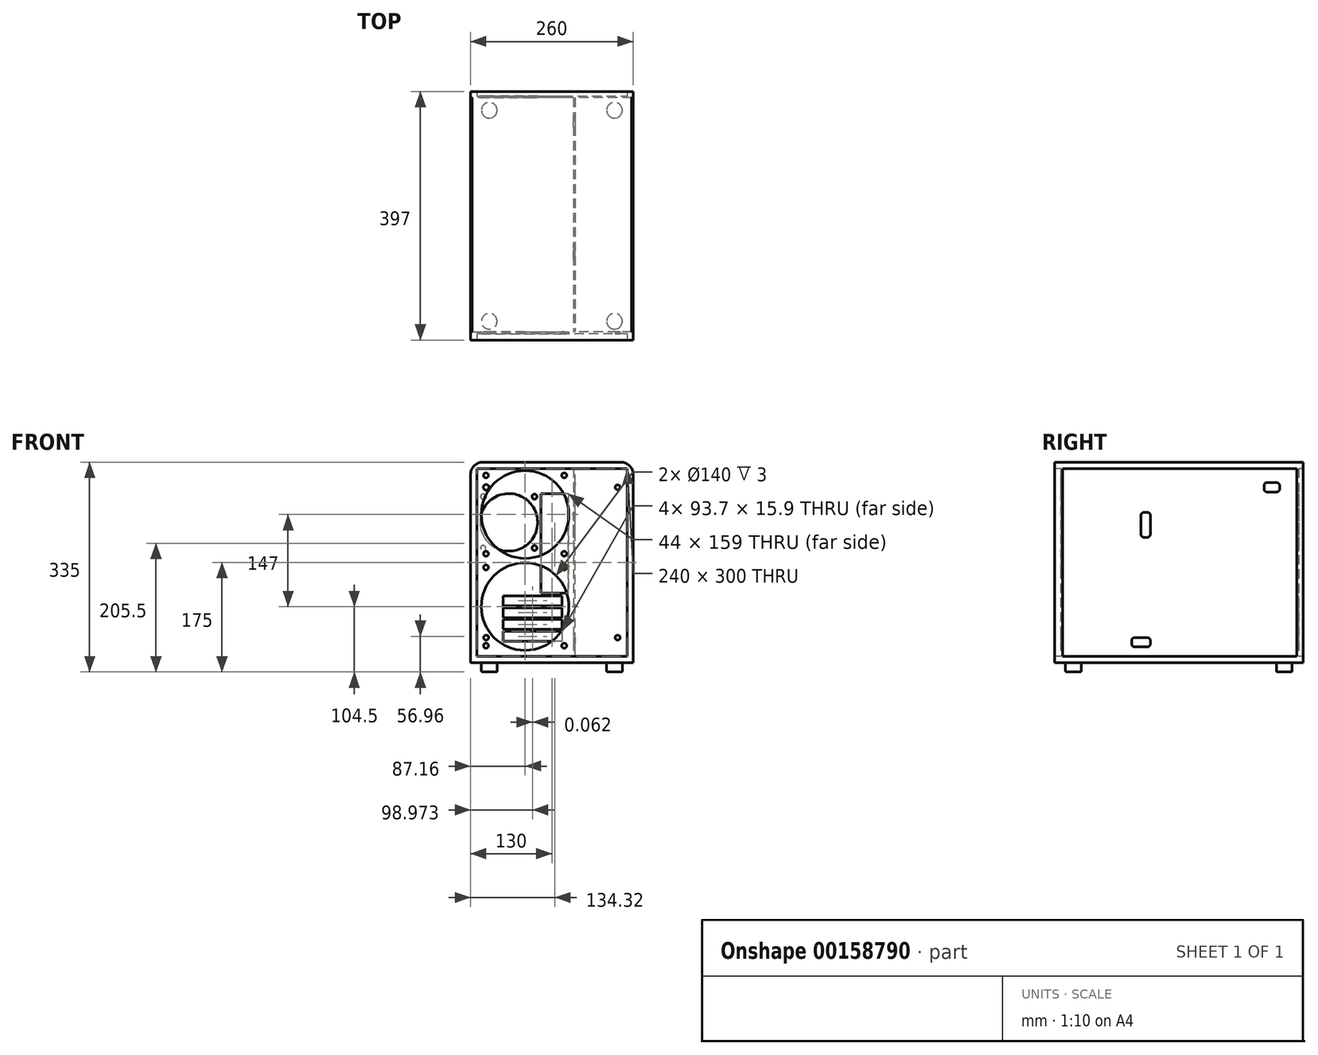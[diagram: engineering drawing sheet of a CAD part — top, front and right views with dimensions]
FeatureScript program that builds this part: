
annotation { "Feature Type Name" : "Feature", "Feature Type Description" : "" }
export const myFeature = defineFeature(function(context is Context, id is Id, definition is map)
    precondition{}
    {
        {
            var Q0;
            Q0=qCreatedBy(makeId("Top.planeOp"),FACE);
            var sketch = newSketch(context, id + "F0", { "sketchPlane" : qUnion([Q0])});
            skLineSegment(sketch, "E0.bottom", {"start": v(130, 198.5) * mm, "end": v(-130, 198.5) * mm});
            skLineSegment(sketch, "E0.top", {"start": v(130, -198.5) * mm, "end": v(-130, -198.5) * mm});
            skLineSegment(sketch, "E0.left", {"start": v(130, 198.5) * mm, "end": v(130, -198.5) * mm});
            skLineSegment(sketch, "E0.right", {"start": v(-130, 198.5) * mm, "end": v(-130, -198.5) * mm});
            skPoint(sketch, "E0.middle", {"position": v(0, 0) * mm});
            skSolve(sketch);
        }
        {
            var Q0;
            Q0=makeQuery(id+"F0.imprint","IMPRINT",FACE,{"disambiguationData":[TD([[makeQuery(id+"F0.imprint","IMPRINT",EDGE,{"derivedFrom":sQuery(id+"F0.wireOp",EDGE,"E0.bottom")}),1.0]])]});
            extrude(context, id + "F1", {"entities" : qUnion([Q0]), "depth" : 320 * mm});
        }
        {
            var Q0;
            Q0=makeQuery(id+"F1.opExtrude","SWEPT_FACE",FACE,{"disambiguationData":[OSD([sQuery(id+"F0.wireOp",EDGE,"E0.top")])]});
            var sketch = newSketch(context, id + "F2", { "sketchPlane" : qUnion([Q0])});
            skLineSegment(sketch, "E1.bottom", {"start": v(120, 310) * mm, "end": v(-120, 310) * mm});
            skLineSegment(sketch, "E1.top", {"start": v(120, 10) * mm, "end": v(-120, 10) * mm});
            skLineSegment(sketch, "E1.left", {"start": v(120, 310) * mm, "end": v(120, 10) * mm});
            skLineSegment(sketch, "E1.right", {"start": v(-120, 310) * mm, "end": v(-120, 10) * mm});
            skPoint(sketch, "E1.middle", {"position": v(0, 160) * mm});
            skSolve(sketch);
        }
        {
            var Q0;
            Q0 = qSketchRegion(id + "F2", true);
            extrude(context, id + "F3", {"entities" : qUnion([Q0]), "operationType" : NewBodyOperationType.REMOVE, "oppositeDirection" : true, "depth" : 506.73 * mm});
        }
        {
            var Q0;
            Q0=makeQuery(id+"F1.opExtrude","SWEPT_FACE",FACE,{"disambiguationData":[OSD([sQuery(id+"F0.wireOp",EDGE,"E0.right")])]});
            var sketch = newSketch(context, id + "F4", { "sketchPlane" : qUnion([Q0])});
            skLineSegment(sketch, "E2.bottom", {"start": v(188.5, 310) * mm, "end": v(-188.5, 310) * mm});
            skLineSegment(sketch, "E2.top", {"start": v(188.5, 10) * mm, "end": v(-188.5, 10) * mm});
            skLineSegment(sketch, "E2.left", {"start": v(188.5, 310) * mm, "end": v(188.5, 10) * mm});
            skLineSegment(sketch, "E2.right", {"start": v(-188.5, 310) * mm, "end": v(-188.5, 10) * mm});
            skPoint(sketch, "E2.middle", {"position": v(0, 160) * mm});
            skLineSegment(sketch, "E3", {"start": v(0, 0) * mm, "end": v(0, 10) * mm});
            skSolve(sketch);
        }
        {
            var Q0;
            Q0 = qSketchRegion(id + "F4", true);
            extrude(context, id + "F5", {"entities" : qUnion([Q0]), "operationType" : NewBodyOperationType.REMOVE, "oppositeDirection" : true, "depth" : 304.8 * mm});
        }
        {
            var Q0;
            Q0=makeQuery(id+"F5.boolean.opBoolean","MERGE",FACE,{"derivedFrom":[makeQuery(id+"F3.boolean.opBoolean","COPY",FACE,{"derivedFrom":makeQuery(id+"F3.opExtrude","SWEPT_FACE",FACE,{"disambiguationData":[OSD([sQuery(id+"F2.wireOp",EDGE,"E1.top")])]})}),makeQuery(id+"F5.opExtrude","SWEPT_FACE",FACE,{"disambiguationData":[OSD([sQuery(id+"F4.wireOp",EDGE,"E2.top")])]})]});
            var sketch = newSketch(context, id + "F6", { "sketchPlane" : qUnion([Q0])});
            skLineSegment(sketch, "E4.bottom", {"start": v(-127.3, -188.5) * mm, "end": v(-124.3, -188.5) * mm});
            skLineSegment(sketch, "E4.top", {"start": v(-127.3, 188.5) * mm, "end": v(-124.3, 188.5) * mm});
            skLineSegment(sketch, "E4.left", {"start": v(-127.3, -188.5) * mm, "end": v(-127.3, 188.5) * mm});
            skLineSegment(sketch, "E4.right", {"start": v(-124.3, -188.5) * mm, "end": v(-124.3, 188.5) * mm});
            skLineSegment(sketch, "E5.bottom", {"start": v(127.32, 188.5) * mm, "end": v(124.32, 188.5) * mm});
            skLineSegment(sketch, "E5.top", {"start": v(127.32, -188.5) * mm, "end": v(124.32, -188.5) * mm});
            skLineSegment(sketch, "E5.left", {"start": v(127.32, 188.5) * mm, "end": v(127.32, -188.5) * mm});
            skLineSegment(sketch, "E5.right", {"start": v(124.32, 188.5) * mm, "end": v(124.32, -188.5) * mm});
            skSolve(sketch);
        }
        {
            var Q0;
            Q0 = qSketchRegion(id + "F6", true);
            extrude(context, id + "F7", {"entities" : qUnion([Q0]), "operationType" : NewBodyOperationType.ADD, "depth" : 300 * mm});
        }
        {
            var Q0;
            Q0=makeQuery(id+"F1.opExtrude","CAP_FACE",FACE,{"disambiguationData":[OSD([sQuery(id+"F0.wireOp",EDGE,"E0.bottom"),sQuery(id+"F0.wireOp",EDGE,"E0.top"),sQuery(id+"F0.wireOp",EDGE,"E0.left"),sQuery(id+"F0.wireOp",EDGE,"E0.right")])],"isStart":true});
            var sketch = newSketch(context, id + "F8", { "sketchPlane" : qUnion([Q0])});
            skCircle(sketch, "E6", {"center": v(-100, 168.5) * mm, "radius": 12.5 * mm});
            skCircle(sketch, "E7", {"center": v(100, 168.5) * mm, "radius": 12.5 * mm});
            skCircle(sketch, "E8", {"center": v(100, -168.5) * mm, "radius": 12.5 * mm});
            skCircle(sketch, "E9", {"center": v(-100, -168.5) * mm, "radius": 12.5 * mm});
            skSolve(sketch);
        }
        {
            var Q0;
            Q0 = qSketchRegion(id + "F8", true);
            extrude(context, id + "F9", {"entities" : qUnion([Q0]), "operationType" : NewBodyOperationType.ADD, "depth" : 15 * mm});
        }
        {
            var Q0;
            Q0=makeQuery(id+"F9.opExtrude","CAP_EDGE",EDGE,{"disambiguationData":[OSD([sQuery(id+"F8.wireOp",EDGE,"E6")])],"isStart":false});
            var Q1;
            Q1=makeQuery(id+"F9.opExtrude","CAP_EDGE",EDGE,{"disambiguationData":[OSD([sQuery(id+"F8.wireOp",EDGE,"E7")])],"isStart":false});
            var Q2;
            Q2=makeQuery(id+"F9.opExtrude","CAP_EDGE",EDGE,{"disambiguationData":[OSD([sQuery(id+"F8.wireOp",EDGE,"E8")])],"isStart":false});
            var Q3;
            Q3=makeQuery(id+"F9.opExtrude","CAP_EDGE",EDGE,{"disambiguationData":[OSD([sQuery(id+"F8.wireOp",EDGE,"E9")])],"isStart":false});
            fillet(context, id + "F10", {"entities" : qUnion([Q0, Q1, Q2, Q3]), "radius" : 2 * mm, "tangentPropagation" : true, "allowEdgeOverflow" : false});
        }
        {
            var Q0;
            {var subQ1=makeQuery(id+"F3.boolean.opBoolean","COPY",FACE,{"derivedFrom":makeQuery(id+"F3.opExtrude","SWEPT_FACE",FACE,{"disambiguationData":[OSD([sQuery(id+"F2.wireOp",EDGE,"E1.top")])]})});var subQ5=makeQuery(id+"F5.opExtrude","SWEPT_FACE",FACE,{"disambiguationData":[OSD([sQuery(id+"F4.wireOp",EDGE,"E2.top")])]});Q0=makeQuery(id+"F7.boolean.opBoolean","SPLIT",FACE,{"disambiguationData":[TD([makeQuery(id+"F1.opExtrude","SWEPT_FACE",FACE,{"disambiguationData":[OSD([sQuery(id+"F0.wireOp",EDGE,"E0.bottom")])]})])],"derivedFrom":makeQuery(id+"F5.boolean.opBoolean","MERGE",FACE,{"derivedFrom":[subQ1,subQ5]})});}
            var sketch = newSketch(context, id + "F11", { "sketchPlane" : qUnion([Q0])});
            skLineSegment(sketch, "E10.bottom", {"start": v(37.32, 188.5) * mm, "end": v(34.32, 188.5) * mm});
            skLineSegment(sketch, "E10.top", {"start": v(37.32, -188.5) * mm, "end": v(34.32, -188.5) * mm});
            skLineSegment(sketch, "E10.left", {"start": v(37.32, 188.5) * mm, "end": v(37.32, -188.5) * mm});
            skLineSegment(sketch, "E10.right", {"start": v(34.32, 188.5) * mm, "end": v(34.32, -188.5) * mm});
            skSolve(sketch);
        }
        {
            var Q0;
            Q0 = qSketchRegion(id + "F11", true);
            extrude(context, id + "F12", {"entities" : qUnion([Q0]), "operationType" : NewBodyOperationType.ADD, "depth" : 300 * mm});
        }
        {
            var Q0;
            Q0=makeQuery(id+"F12.opExtrude","SWEPT_FACE",FACE,{"disambiguationData":[OSD([sQuery(id+"F11.wireOp",EDGE,"E10.left")])]});
            var sketch = newSketch(context, id + "F13", { "sketchPlane" : qUnion([Q0])});
            skLineSegment(sketch, "E11.bottom", {"start": v(-188.5, 10) * mm, "end": v(-185.5, 10) * mm});
            skLineSegment(sketch, "E11.top", {"start": v(-188.5, 310) * mm, "end": v(-185.5, 310) * mm});
            skLineSegment(sketch, "E11.left", {"start": v(-188.5, 10) * mm, "end": v(-188.5, 310) * mm});
            skLineSegment(sketch, "E11.right", {"start": v(-185.5, 10) * mm, "end": v(-185.5, 310) * mm});
            skSolve(sketch);
        }
        {
            var Q0;
            Q0 = qSketchRegion(id + "F13", true);
            extrude(context, id + "F14", {"entities" : qUnion([Q0]), "operationType" : NewBodyOperationType.ADD, "depth" : 87 * mm});
        }
        {
            var Q0;
            Q0=makeQuery(id+"F12.opExtrude","SWEPT_FACE",FACE,{"disambiguationData":[OSD([sQuery(id+"F11.wireOp",EDGE,"E10.right")])]});
            var sketch = newSketch(context, id + "F15", { "sketchPlane" : qUnion([Q0])});
            skLineSegment(sketch, "E12.bottom", {"start": v(158.5, 10) * mm, "end": v(155.5, 10) * mm});
            skLineSegment(sketch, "E12.top", {"start": v(158.5, 310) * mm, "end": v(155.5, 310) * mm});
            skLineSegment(sketch, "E12.left", {"start": v(158.5, 10) * mm, "end": v(158.5, 310) * mm});
            skLineSegment(sketch, "E12.right", {"start": v(155.5, 10) * mm, "end": v(155.5, 310) * mm});
            skSolve(sketch);
        }
        {
            var Q0;
            Q0 = qSketchRegion(id + "F15", true);
            extrude(context, id + "F16", {"entities" : qUnion([Q0]), "operationType" : NewBodyOperationType.ADD, "depth" : 160 * mm});
        }
        {
            var Q0;
            Q0=makeQuery(id+"F16.opExtrude","SWEPT_FACE",FACE,{"disambiguationData":[OSD([sQuery(id+"F15.wireOp",EDGE,"E12.left")])]});
            var sketch = newSketch(context, id + "F17", { "sketchPlane" : qUnion([Q0])});
            skPoint(sketch, "E13.middle", {"position": v(-42.85, 236.5) * mm});
            skCircle(sketch, "E14", {"center": v(-105.35, 299) * mm, "radius": 4 * mm});
            skCircle(sketch, "E15", {"center": v(19.65, 299) * mm, "radius": 4 * mm});
            skCircle(sketch, "E16", {"center": v(-105.35, 174) * mm, "radius": 4 * mm});
            skCircle(sketch, "E17", {"center": v(19.65, 174) * mm, "radius": 4 * mm});
            skCircle(sketch, "E18", {"center": v(-42.85, 236.5) * mm, "radius": 70 * mm});
            skCircle(sketch, "E19", {"center": v(-42.85, 83.5) * mm, "radius": 70 * mm});
            skCircle(sketch, "E20", {"center": v(19.65, 146) * mm, "radius": 4 * mm});
            skCircle(sketch, "E21", {"center": v(19.65, 21) * mm, "radius": 4 * mm});
            skCircle(sketch, "E22", {"center": v(-105.35, 21) * mm, "radius": 4 * mm});
            skCircle(sketch, "E23", {"center": v(-105.35, 146) * mm, "radius": 4 * mm});
            skSolve(sketch);
        }
        {
            var Q0;
            Q0 = qSketchRegion(id + "F17", true);
            extrude(context, id + "F18", {"entities" : qUnion([Q0]), "operationType" : NewBodyOperationType.REMOVE, "oppositeDirection" : true, "depth" : 10 * mm});
        }
        {
            var Q0;
            Q0=makeQuery(id+"F16.boolean.opBoolean","SPLIT",FACE,{"disambiguationData":[TD([makeQuery(id+"F16.opExtrude","SWEPT_FACE",FACE,{"disambiguationData":[OSD([sQuery(id+"F15.wireOp",EDGE,"E12.right")])]})])],"derivedFrom":makeQuery(id+"F7.opExtrude","SWEPT_FACE",FACE,{"disambiguationData":[OSD([sQuery(id+"F6.wireOp",EDGE,"E4.right")])]})});
            var sketch = newSketch(context, id + "F19", { "sketchPlane" : qUnion([Q0])});
            skLineSegment(sketch, "E24.bottom", {"start": v(-155.5, 10) * mm, "end": v(188.5, 10) * mm});
            skLineSegment(sketch, "E24.top", {"start": v(-155.5, 310) * mm, "end": v(188.5, 310) * mm});
            skLineSegment(sketch, "E24.left", {"start": v(-155.5, 10) * mm, "end": v(-155.5, 310) * mm});
            skLineSegment(sketch, "E24.right", {"start": v(188.5, 10) * mm, "end": v(188.5, 310) * mm});
            skSolve(sketch);
        }
        {
            var Q0;
            Q0 = qSketchRegion(id + "F19", true);
            extrude(context, id + "F20", {"entities" : qUnion([Q0]), "operationType" : NewBodyOperationType.REMOVE, "oppositeDirection" : true, "depth" : 206 * mm});
        }
        {
            var Q0;
            {var subQ3=makeQuery(id+"F3.boolean.opBoolean","COPY",FACE,{"derivedFrom":makeQuery(id+"F3.opExtrude","SWEPT_FACE",FACE,{"disambiguationData":[OSD([sQuery(id+"F2.wireOp",EDGE,"E1.top")])]})});var subQ7=makeQuery(id+"F5.opExtrude","SWEPT_FACE",FACE,{"disambiguationData":[OSD([sQuery(id+"F4.wireOp",EDGE,"E2.top")])]});var subQ10=makeQuery(id+"F1.opExtrude","SWEPT_FACE",FACE,{"disambiguationData":[OSD([sQuery(id+"F0.wireOp",EDGE,"E0.bottom")])]});var subQ12=makeQuery(id+"F1.opExtrude","SWEPT_FACE",FACE,{"disambiguationData":[OSD([sQuery(id+"F0.wireOp",EDGE,"E0.right")])]});var subQ16=makeQuery(id+"F5.boolean.opBoolean","MERGE",FACE,{"derivedFrom":[subQ3,subQ7]});Q0=makeQuery(id+"F20.boolean.opBoolean","MERGE",FACE,{"derivedFrom":[makeQuery(id+"F7.boolean.opBoolean","SPLIT",FACE,{"disambiguationData":[TD([subQ12])],"derivedFrom":subQ16}),makeQuery(id+"F16.boolean.opBoolean","SPLIT",FACE,{"disambiguationData":[TD([subQ10])],"derivedFrom":makeQuery(id+"F7.boolean.opBoolean","SPLIT",FACE,{"disambiguationData":[TD([subQ10])],"derivedFrom":subQ16})}),makeQuery(id+"F20.opExtrude","SWEPT_FACE",FACE,{"disambiguationData":[OSD([sQuery(id+"F19.wireOp",EDGE,"E24.bottom")])]})]});}
            var sketch = newSketch(context, id + "F21", { "sketchPlane" : qUnion([Q0])});
            skLineSegment(sketch, "E25", {"start": v(120, 188.5) * mm, "end": v(-120, 188.5) * mm});
            skLineSegment(sketch, "E26", {"start": v(-120, 188.5) * mm, "end": v(-120, 191.5) * mm});
            skLineSegment(sketch, "E27", {"start": v(-120, 191.5) * mm, "end": v(120, 191.5) * mm});
            skLineSegment(sketch, "E28", {"start": v(120, 191.5) * mm, "end": v(120, 188.5) * mm});
            skSolve(sketch);
        }
        {
            var Q0;
            Q0 = qSketchRegion(id + "F21", true);
            extrude(context, id + "F22", {"entities" : qUnion([Q0]), "operationType" : NewBodyOperationType.ADD, "depth" : 300 * mm});
        }
        {
            var Q0;
            {var subQ3=sQuery(id+"F0.wireOp",EDGE,"E0.right");var subQ4=makeQuery(id+"F1.opExtrude","SWEPT_FACE",FACE,{"disambiguationData":[OSD([subQ3])]});var subQ6=makeQuery(id+"F3.boolean.opBoolean","COPY",FACE,{"derivedFrom":makeQuery(id+"F3.opExtrude","SWEPT_FACE",FACE,{"disambiguationData":[OSD([sQuery(id+"F2.wireOp",EDGE,"E1.right")])]})});var subQ7=makeQuery(id+"F5.boolean.opBoolean","COPY",FACE,{"disambiguationData":[TD([subQ4])],"derivedFrom":makeQuery(id+"F5.opExtrude","SWEPT_FACE",FACE,{"disambiguationData":[OSD([sQuery(id+"F4.wireOp",EDGE,"E2.right")])]})});Q0=makeQuery(id+"F22.boolean.opBoolean","MERGE",FACE,{"derivedFrom":[makeQuery(id+"F20.boolean.opBoolean","MERGE",FACE,{"derivedFrom":[makeQuery(id+"F7.boolean.opBoolean","SPLIT",FACE,{"disambiguationData":[TD([subQ6])],"derivedFrom":subQ7}),makeQuery(id+"F7.boolean.opBoolean","SPLIT",FACE,{"disambiguationData":[TD([subQ4])],"derivedFrom":subQ7}),makeQuery(id+"F20.opExtrude","SWEPT_FACE",FACE,{"disambiguationData":[OSD([sQuery(id+"F19.wireOp",EDGE,"E24.right")])]})]}),makeQuery(id+"F22.opExtrude","SWEPT_FACE",FACE,{"disambiguationData":[OSD([sQuery(id+"F21.wireOp",EDGE,"E25")])]})]});}
            var sketch = newSketch(context, id + "F23", { "sketchPlane" : qUnion([Q0])});
            skLineSegment(sketch, "E29.bottom", {"start": v(26.32, 270) * mm, "end": v(-17.68, 270) * mm});
            skLineSegment(sketch, "E29.top", {"start": v(26.32, 111) * mm, "end": v(-17.68, 111) * mm});
            skLineSegment(sketch, "E29.left", {"start": v(26.32, 270) * mm, "end": v(26.32, 111) * mm});
            skLineSegment(sketch, "E29.right", {"start": v(-17.68, 270) * mm, "end": v(-17.68, 111) * mm});
            skLineSegment(sketch, "E30", {"start": v(16.01, 106.61) * mm, "end": v(16.01, 90.71) * mm});
            skLineSegment(sketch, "E31", {"start": v(16.01, 106.61) * mm, "end": v(-77.69, 106.61) * mm});
            skLineSegment(sketch, "E32", {"start": v(16.01, 90.71) * mm, "end": v(-77.69, 90.71) * mm});
            skLineSegment(sketch, "E33", {"start": v(-77.69, 90.71) * mm, "end": v(-77.69, 106.61) * mm});
            skLineSegment(sketch, "E34.1.0.0", {"start": v(15.95, 87.71) * mm, "end": v(-77.75, 87.71) * mm});
            skLineSegment(sketch, "E34.1.0.1", {"start": v(-77.75, 71.81) * mm, "end": v(-77.75, 87.71) * mm});
            skLineSegment(sketch, "E34.1.0.2", {"start": v(15.95, 71.81) * mm, "end": v(-77.75, 71.81) * mm});
            skLineSegment(sketch, "E34.1.0.3", {"start": v(15.95, 87.71) * mm, "end": v(15.95, 71.81) * mm});
            skLineSegment(sketch, "E34.2.0.0", {"start": v(15.89, 68.81) * mm, "end": v(-77.81, 68.81) * mm});
            skLineSegment(sketch, "E34.2.0.1", {"start": v(-77.81, 52.91) * mm, "end": v(-77.81, 68.81) * mm});
            skLineSegment(sketch, "E34.2.0.2", {"start": v(15.89, 52.91) * mm, "end": v(-77.81, 52.91) * mm});
            skLineSegment(sketch, "E34.2.0.3", {"start": v(15.89, 68.81) * mm, "end": v(15.89, 52.91) * mm});
            skLineSegment(sketch, "E34.3.0.0", {"start": v(15.82, 49.91) * mm, "end": v(-77.88, 49.91) * mm});
            skLineSegment(sketch, "E34.3.0.1", {"start": v(-77.88, 34.01) * mm, "end": v(-77.88, 49.91) * mm});
            skLineSegment(sketch, "E34.3.0.2", {"start": v(15.82, 34.01) * mm, "end": v(-77.88, 34.01) * mm});
            skLineSegment(sketch, "E34.3.0.3", {"start": v(15.82, 49.91) * mm, "end": v(15.82, 34.01) * mm});
            skLineSegment(sketch, "E34.direction1", {"start": v(-77.69, 90.71) * mm, "end": v(-77.75, 71.81) * mm, "construction": true});
            skLineSegment(sketch, "E35", {"start": v(-77.69, 90.71) * mm, "end": v(-77.75, 87.71) * mm});
            skLineSegment(sketch, "E36", {"start": v(26.32, 111) * mm, "end": v(26.32, 89.64) * mm});
            skLineSegment(sketch, "E37", {"start": v(16.01, 106.61) * mm, "end": v(26.32, 106.61) * mm});
            skSolve(sketch);
        }
        {
            var Q0;
            Q0 = qSketchRegion(id + "F23", true);
            extrude(context, id + "F24", {"entities" : qUnion([Q0]), "operationType" : NewBodyOperationType.REMOVE, "oppositeDirection" : true, "depth" : 25 * mm});
        }
        {
            var Q0;
            Q0=makeQuery(id+"F22.opExtrude","SWEPT_FACE",FACE,{"disambiguationData":[OSD([sQuery(id+"F21.wireOp",EDGE,"E27")])]});
            var sketch = newSketch(context, id + "F25", { "sketchPlane" : qUnion([Q0])});
            skPoint(sketch, "E38.middle", {"position": v(68.84, 224) * mm});
            skCircle(sketch, "E39", {"center": v(27.84, 265) * mm, "radius": 4 * mm});
            skCircle(sketch, "E40", {"center": v(109.84, 265) * mm, "radius": 4 * mm});
            skCircle(sketch, "E41", {"center": v(27.84, 183) * mm, "radius": 4 * mm});
            skCircle(sketch, "E42", {"center": v(109.84, 183) * mm, "radius": 4 * mm});
            skCircle(sketch, "E43", {"center": v(68.84, 224) * mm, "radius": 46 * mm});
            skSolve(sketch);
        }
        {
            var Q0;
            Q0 = qSketchRegion(id + "F25", true);
            extrude(context, id + "F26", {"entities" : qUnion([Q0]), "operationType" : NewBodyOperationType.REMOVE, "oppositeDirection" : true, "depth" : 25 * mm});
        }
        {
            var Q0;
            {var subQ3=sQuery(id+"F0.wireOp",EDGE,"E0.right");var subQ4=makeQuery(id+"F1.opExtrude","SWEPT_FACE",FACE,{"disambiguationData":[OSD([subQ3])]});var subQ6=makeQuery(id+"F3.boolean.opBoolean","COPY",FACE,{"derivedFrom":makeQuery(id+"F3.opExtrude","SWEPT_FACE",FACE,{"disambiguationData":[OSD([sQuery(id+"F2.wireOp",EDGE,"E1.right")])]})});var subQ7=makeQuery(id+"F5.boolean.opBoolean","COPY",FACE,{"disambiguationData":[TD([subQ4])],"derivedFrom":makeQuery(id+"F5.opExtrude","SWEPT_FACE",FACE,{"disambiguationData":[OSD([sQuery(id+"F4.wireOp",EDGE,"E2.right")])]})});Q0=makeQuery(id+"F22.boolean.opBoolean","MERGE",FACE,{"derivedFrom":[makeQuery(id+"F20.boolean.opBoolean","MERGE",FACE,{"derivedFrom":[makeQuery(id+"F7.boolean.opBoolean","SPLIT",FACE,{"disambiguationData":[TD([subQ6])],"derivedFrom":subQ7}),makeQuery(id+"F7.boolean.opBoolean","SPLIT",FACE,{"disambiguationData":[TD([subQ4])],"derivedFrom":subQ7}),makeQuery(id+"F20.opExtrude","SWEPT_FACE",FACE,{"disambiguationData":[OSD([sQuery(id+"F19.wireOp",EDGE,"E24.right")])]})]}),makeQuery(id+"F22.opExtrude","SWEPT_FACE",FACE,{"disambiguationData":[OSD([sQuery(id+"F21.wireOp",EDGE,"E25")])]})]});}
            var sketch = newSketch(context, id + "F27", { "sketchPlane" : qUnion([Q0])});
            skLineSegment(sketch, "E44.bottom", {"start": v(-130, 10) * mm, "end": v(-127, 10) * mm});
            skLineSegment(sketch, "E44.top", {"start": v(-130, 310) * mm, "end": v(-127, 310) * mm});
            skLineSegment(sketch, "E44.left", {"start": v(-130, 10) * mm, "end": v(-130, 310) * mm});
            skLineSegment(sketch, "E44.right", {"start": v(-127, 10) * mm, "end": v(-127, 310) * mm});
            skSolve(sketch);
        }
        {
            var Q0;
            Q0 = qSketchRegion(id + "F27", true);
            extrude(context, id + "F28", {"entities" : qUnion([Q0]), "operationType" : NewBodyOperationType.REMOVE, "depth" : 377 * mm});
        }
        {
            var Q0;
            Q0=makeQuery(id+"F28.boolean.opBoolean","COPY",FACE,{"derivedFrom":makeQuery(id+"F28.opExtrude","SWEPT_FACE",FACE,{"disambiguationData":[OSD([sQuery(id+"F27.wireOp",EDGE,"E44.right")])]})});
            var sketch = newSketch(context, id + "F29", { "sketchPlane" : qUnion([Q0])});
            skLineSegment(sketch, "E45.right", {"start": v(158.5, 310) * mm, "end": v(158.5, 10) * mm});
            skLineSegment(sketch, "E46.bottom", {"start": v(158.5, 10) * mm, "end": v(188.5, 10) * mm});
            skLineSegment(sketch, "E46.top", {"start": v(158.5, 310) * mm, "end": v(188.5, 310) * mm});
            skLineSegment(sketch, "E46.right", {"start": v(188.5, 10) * mm, "end": v(188.5, 310) * mm});
            skSolve(sketch);
        }
        {
            var Q0;
            Q0 = qSketchRegion(id + "F29", true);
            extrude(context, id + "F30", {"entities" : qUnion([Q0]), "operationType" : NewBodyOperationType.REMOVE, "oppositeDirection" : true, "depth" : 25 * mm});
        }
        {
            var Q0;
            Q0=makeQuery(id+"F20.boolean.opBoolean","MERGE",FACE,{"derivedFrom":[makeQuery(id+"F16.opExtrude","SWEPT_FACE",FACE,{"disambiguationData":[OSD([sQuery(id+"F15.wireOp",EDGE,"E12.right")])]}),makeQuery(id+"F20.opExtrude","SWEPT_FACE",FACE,{"disambiguationData":[OSD([sQuery(id+"F19.wireOp",EDGE,"E24.left")])]})]});
            var sketch = newSketch(context, id + "F31", { "sketchPlane" : qUnion([Q0])});
            skLineSegment(sketch, "E47.bottom", {"start": v(127, 310) * mm, "end": v(-34.32, 310) * mm});
            skLineSegment(sketch, "E47.top", {"start": v(127, 10) * mm, "end": v(-34.32, 10) * mm});
            skLineSegment(sketch, "E47.left", {"start": v(127, 310) * mm, "end": v(127, 10) * mm});
            skLineSegment(sketch, "E47.right", {"start": v(-34.32, 310) * mm, "end": v(-34.32, 10) * mm});
            skSolve(sketch);
        }
        {
            var Q0;
            Q0 = qSketchRegion(id + "F31", true);
            extrude(context, id + "F32", {"entities" : qUnion([Q0]), "operationType" : NewBodyOperationType.REMOVE, "oppositeDirection" : true, "depth" : 25 * mm});
        }
        {
            var Q0;
            {var subQ2=makeQuery(id+"F3.boolean.opBoolean","COPY",FACE,{"derivedFrom":makeQuery(id+"F3.opExtrude","SWEPT_FACE",FACE,{"disambiguationData":[OSD([sQuery(id+"F2.wireOp",EDGE,"E1.top")])]})});var subQ4=makeQuery(id+"F1.opExtrude","SWEPT_FACE",FACE,{"disambiguationData":[OSD([sQuery(id+"F0.wireOp",EDGE,"E0.right")])]});var subQ6=makeQuery(id+"F5.opExtrude","SWEPT_FACE",FACE,{"disambiguationData":[OSD([sQuery(id+"F4.wireOp",EDGE,"E2.top")])]});var subQ18=makeQuery(id+"F1.opExtrude","SWEPT_FACE",FACE,{"disambiguationData":[OSD([sQuery(id+"F0.wireOp",EDGE,"E0.bottom")])]});var subQ19=makeQuery(id+"F1.opExtrude","SWEPT_FACE",FACE,{"disambiguationData":[OSD([sQuery(id+"F0.wireOp",EDGE,"E0.top")])]});var subQ20=makeQuery(id+"F5.boolean.opBoolean","MERGE",FACE,{"derivedFrom":[subQ2,subQ6]});var subQ21=makeQuery(id+"F7.boolean.opBoolean","SPLIT",FACE,{"disambiguationData":[TD([subQ18])],"derivedFrom":subQ20});Q0=makeQuery(id+"F32.boolean.opBoolean","MERGE",FACE,{"derivedFrom":[makeQuery(id+"F30.boolean.opBoolean","MERGE",FACE,{"derivedFrom":[makeQuery(id+"F16.boolean.opBoolean","SPLIT",FACE,{"disambiguationData":[TD([subQ19])],"derivedFrom":subQ21}),makeQuery(id+"F28.boolean.opBoolean","MERGE",FACE,{"derivedFrom":[makeQuery(id+"F22.boolean.opBoolean","SPLIT",FACE,{"disambiguationData":[TD([subQ4])],"derivedFrom":makeQuery(id+"F20.boolean.opBoolean","MERGE",FACE,{"derivedFrom":[makeQuery(id+"F7.boolean.opBoolean","SPLIT",FACE,{"disambiguationData":[TD([subQ4])],"derivedFrom":subQ20}),makeQuery(id+"F16.boolean.opBoolean","SPLIT",FACE,{"disambiguationData":[TD([subQ18])],"derivedFrom":subQ21}),makeQuery(id+"F20.opExtrude","SWEPT_FACE",FACE,{"disambiguationData":[OSD([sQuery(id+"F19.wireOp",EDGE,"E24.bottom")])]})]})}),makeQuery(id+"F28.opExtrude","SWEPT_FACE",FACE,{"disambiguationData":[OSD([sQuery(id+"F27.wireOp",EDGE,"E44.bottom")])]})]}),makeQuery(id+"F30.opExtrude","SWEPT_FACE",FACE,{"disambiguationData":[OSD([sQuery(id+"F29.wireOp",EDGE,"E46.bottom")])]})]}),makeQuery(id+"F32.opExtrude","SWEPT_FACE",FACE,{"disambiguationData":[OSD([sQuery(id+"F31.wireOp",EDGE,"E47.top")])]})]});}
            var sketch = newSketch(context, id + "F33", { "sketchPlane" : qUnion([Q0])});
            skLineSegment(sketch, "E48.bottom", {"start": v(-130, -188.5) * mm, "end": v(34.32, -188.5) * mm});
            skLineSegment(sketch, "E48.top", {"start": v(-130, -185.5) * mm, "end": v(34.32, -185.5) * mm});
            skLineSegment(sketch, "E48.left", {"start": v(-130, -188.5) * mm, "end": v(-130, -185.5) * mm});
            skLineSegment(sketch, "E48.right", {"start": v(34.32, -188.5) * mm, "end": v(34.32, -185.5) * mm});
            skSolve(sketch);
        }
        {
            var Q0;
            Q0 = qSketchRegion(id + "F33", true);
            extrude(context, id + "F34", {"entities" : qUnion([Q0]), "operationType" : NewBodyOperationType.ADD, "depth" : 300 * mm});
        }
        {
            var Q0;
            Q0=makeQuery(id+"F1.opExtrude","CAP_EDGE",EDGE,{"disambiguationData":[OSD([sQuery(id+"F0.wireOp",EDGE,"E0.right")])],"isStart":false});
            fillet(context, id + "F35", {"entities" : qUnion([Q0]), "radius" : 20 * mm, "tangentPropagation" : true, "allowEdgeOverflow" : false});
        }
        {
            var Q0;
            Q0=makeQuery(id+"F34.boolean.opBoolean","MERGE",FACE,{"derivedFrom":[makeQuery(id+"F14.boolean.opBoolean","MERGE",FACE,{"derivedFrom":[makeQuery(id+"F12.opExtrude","SWEPT_FACE",FACE,{"disambiguationData":[OSD([sQuery(id+"F11.wireOp",EDGE,"E10.top")])]}),makeQuery(id+"F14.opExtrude","SWEPT_FACE",FACE,{"disambiguationData":[OSD([sQuery(id+"F13.wireOp",EDGE,"E11.left")])]})]}),makeQuery(id+"F34.opExtrude","SWEPT_FACE",FACE,{"disambiguationData":[OSD([sQuery(id+"F33.wireOp",EDGE,"E48.bottom")])]})]});
            var sketch = newSketch(context, id + "F36", { "sketchPlane" : qUnion([Q0])});
            skPoint(sketch, "E49.middle", {"position": v(-42.84, 236.5) * mm});
            skCircle(sketch, "E50", {"center": v(-42.84, 236.5) * mm, "radius": 70 * mm});
            skCircle(sketch, "E51", {"center": v(-105.34, 299) * mm, "radius": 4 * mm});
            skCircle(sketch, "E52", {"center": v(19.66, 299) * mm, "radius": 4 * mm});
            skCircle(sketch, "E53", {"center": v(-105.34, 174) * mm, "radius": 4 * mm});
            skCircle(sketch, "E54", {"center": v(19.66, 174) * mm, "radius": 4 * mm});
            skCircle(sketch, "E55", {"center": v(-42.84, 89.5) * mm, "radius": 70 * mm});
            skCircle(sketch, "E56", {"center": v(-105.34, 152) * mm, "radius": 4 * mm});
            skCircle(sketch, "E57", {"center": v(19.66, 152) * mm, "radius": 4 * mm});
            skCircle(sketch, "E58", {"center": v(19.66, 27) * mm, "radius": 4 * mm});
            skCircle(sketch, "E59", {"center": v(-105.34, 27) * mm, "radius": 4 * mm});
            skSolve(sketch);
        }
        {
            var Q0;
            Q0 = qSketchRegion(id + "F36", true);
            extrude(context, id + "F37", {"entities" : qUnion([Q0]), "operationType" : NewBodyOperationType.REMOVE, "oppositeDirection" : true, "depth" : 25 * mm});
        }
        {
            var Q0;
            Q0=makeQuery(id+"F7.opExtrude","SWEPT_FACE",FACE,{"disambiguationData":[OSD([sQuery(id+"F6.wireOp",EDGE,"E5.left")])]});
            var sketch = newSketch(context, id + "F38", { "sketchPlane" : qUnion([Q0])});
            skLineSegment(sketch, "E60.bottom", {"start": v(-188.5, 310) * mm, "end": v(188.5, 310) * mm});
            skLineSegment(sketch, "E60.top", {"start": v(-188.5, 10) * mm, "end": v(188.5, 10) * mm});
            skLineSegment(sketch, "E60.left", {"start": v(-188.5, 310) * mm, "end": v(-188.5, 10) * mm});
            skLineSegment(sketch, "E60.right", {"start": v(188.5, 310) * mm, "end": v(188.5, 10) * mm});
            skSolve(sketch);
        }
        {
            var Q0;
            Q0 = qSketchRegion(id + "F38", true);
            extrude(context, id + "F39", {"entities" : qUnion([Q0]), "operationType" : NewBodyOperationType.REMOVE, "oppositeDirection" : true, "depth" : 3 * mm});
        }
        {
            var Q0;
            {var subQ3=makeQuery(id+"F1.opExtrude","SWEPT_FACE",FACE,{"disambiguationData":[OSD([sQuery(id+"F0.wireOp",EDGE,"E0.left")])]});Q0=makeQuery(id+"F39.boolean.opBoolean","MERGE",FACE,{"derivedFrom":[makeQuery(id+"F7.boolean.opBoolean","SPLIT",FACE,{"disambiguationData":[TD([subQ3])],"derivedFrom":makeQuery(id+"F5.boolean.opBoolean","COPY",FACE,{"disambiguationData":[TD([subQ3])],"derivedFrom":makeQuery(id+"F5.opExtrude","SWEPT_FACE",FACE,{"disambiguationData":[OSD([sQuery(id+"F4.wireOp",EDGE,"E2.left")])]})})}),makeQuery(id+"F39.opExtrude","SWEPT_FACE",FACE,{"disambiguationData":[OSD([sQuery(id+"F38.wireOp",EDGE,"E60.left")])]})]});}
            var sketch = newSketch(context, id + "F40", { "sketchPlane" : qUnion([Q0])});
            skLineSegment(sketch, "E61.bottom", {"start": v(-124.32, 310) * mm, "end": v(-130, 310) * mm});
            skLineSegment(sketch, "E61.top", {"start": v(-124.32, 10) * mm, "end": v(-130, 10) * mm});
            skLineSegment(sketch, "E61.left", {"start": v(-124.32, 310) * mm, "end": v(-124.32, 10) * mm});
            skLineSegment(sketch, "E61.right", {"start": v(-130, 310) * mm, "end": v(-130, 10) * mm});
            skSolve(sketch);
        }
        {
            var Q0;
            Q0 = qSketchRegion(id + "F40", true);
            extrude(context, id + "F41", {"entities" : qUnion([Q0]), "operationType" : NewBodyOperationType.ADD, "depth" : 3 * mm});
        }
        {
            var Q0;
            Q0=makeQuery(id+"F1.opExtrude","CAP_EDGE",EDGE,{"disambiguationData":[OSD([sQuery(id+"F0.wireOp",EDGE,"E0.left")])],"isStart":false});
            fillet(context, id + "F42", {"entities" : qUnion([Q0]), "radius" : 20 * mm, "tangentPropagation" : true, "allowEdgeOverflow" : false});
        }
        {
            var Q0;
            {var subQ3=makeQuery(id+"F3.boolean.opBoolean","COPY",FACE,{"derivedFrom":makeQuery(id+"F3.opExtrude","SWEPT_FACE",FACE,{"disambiguationData":[OSD([sQuery(id+"F2.wireOp",EDGE,"E1.bottom")])]})});var subQ4=makeQuery(id+"F1.opExtrude","SWEPT_FACE",FACE,{"disambiguationData":[OSD([sQuery(id+"F0.wireOp",EDGE,"E0.right")])]});var subQ5=makeQuery(id+"F5.opExtrude","SWEPT_FACE",FACE,{"disambiguationData":[OSD([sQuery(id+"F4.wireOp",EDGE,"E2.bottom")])]});var subQ20=makeQuery(id+"F1.opExtrude","SWEPT_FACE",FACE,{"disambiguationData":[OSD([sQuery(id+"F0.wireOp",EDGE,"E0.bottom")])]});var subQ21=makeQuery(id+"F1.opExtrude","SWEPT_FACE",FACE,{"disambiguationData":[OSD([sQuery(id+"F0.wireOp",EDGE,"E0.top")])]});var subQ22=makeQuery(id+"F5.boolean.opBoolean","MERGE",FACE,{"derivedFrom":[subQ3,subQ5]});var subQ23=makeQuery(id+"F7.boolean.opBoolean","SPLIT",FACE,{"disambiguationData":[TD([subQ20])],"derivedFrom":subQ22});Q0=makeQuery(id+"F34.boolean.opBoolean","SPLIT",FACE,{"disambiguationData":[TD([subQ4])],"derivedFrom":makeQuery(id+"F32.boolean.opBoolean","MERGE",FACE,{"derivedFrom":[makeQuery(id+"F30.boolean.opBoolean","MERGE",FACE,{"derivedFrom":[makeQuery(id+"F16.boolean.opBoolean","SPLIT",FACE,{"disambiguationData":[TD([subQ21])],"derivedFrom":subQ23}),makeQuery(id+"F28.boolean.opBoolean","MERGE",FACE,{"derivedFrom":[makeQuery(id+"F22.boolean.opBoolean","SPLIT",FACE,{"disambiguationData":[TD([subQ4])],"derivedFrom":makeQuery(id+"F20.boolean.opBoolean","MERGE",FACE,{"derivedFrom":[makeQuery(id+"F7.boolean.opBoolean","SPLIT",FACE,{"disambiguationData":[TD([subQ4])],"derivedFrom":subQ22}),makeQuery(id+"F16.boolean.opBoolean","SPLIT",FACE,{"disambiguationData":[TD([subQ20])],"derivedFrom":subQ23}),makeQuery(id+"F20.opExtrude","SWEPT_FACE",FACE,{"disambiguationData":[OSD([sQuery(id+"F19.wireOp",EDGE,"E24.top")])]})]})}),makeQuery(id+"F28.opExtrude","SWEPT_FACE",FACE,{"disambiguationData":[OSD([sQuery(id+"F27.wireOp",EDGE,"E44.top")])]})]}),makeQuery(id+"F30.opExtrude","SWEPT_FACE",FACE,{"disambiguationData":[OSD([sQuery(id+"F29.wireOp",EDGE,"E46.top")])]})]}),makeQuery(id+"F32.opExtrude","SWEPT_FACE",FACE,{"disambiguationData":[OSD([sQuery(id+"F31.wireOp",EDGE,"E47.bottom")])]})]})});}
            var sketch = newSketch(context, id + "F43", { "sketchPlane" : qUnion([Q0])});
            skLineSegment(sketch, "E62.bottom", {"start": v(-127.32, -188.5) * mm, "end": v(-124.32, -188.5) * mm});
            skLineSegment(sketch, "E62.top", {"start": v(-127.32, 185.5) * mm, "end": v(-124.32, 185.5) * mm});
            skLineSegment(sketch, "E62.left", {"start": v(-127.32, -188.5) * mm, "end": v(-127.32, 185.5) * mm});
            skLineSegment(sketch, "E62.right", {"start": v(-124.32, -188.5) * mm, "end": v(-124.32, 185.5) * mm});
            skSolve(sketch);
        }
        {
            var Q0;
            Q0 = qSketchRegion(id + "F43", true);
            extrude(context, id + "F44", {"entities" : qUnion([Q0]), "depth" : 300 * mm});
        }
        {
            var Q0;
            {var subQ2=makeQuery(id+"F7.opExtrude","SWEPT_FACE",FACE,{"disambiguationData":[OSD([sQuery(id+"F6.wireOp",EDGE,"E5.right")])]});var subQ5=makeQuery(id+"F3.boolean.opBoolean","COPY",FACE,{"derivedFrom":makeQuery(id+"F3.opExtrude","SWEPT_FACE",FACE,{"disambiguationData":[OSD([sQuery(id+"F2.wireOp",EDGE,"E1.bottom")])]})});var subQ6=makeQuery(id+"F1.opExtrude","SWEPT_FACE",FACE,{"disambiguationData":[OSD([sQuery(id+"F0.wireOp",EDGE,"E0.left")])]});var subQ7=makeQuery(id+"F5.opExtrude","SWEPT_FACE",FACE,{"disambiguationData":[OSD([sQuery(id+"F4.wireOp",EDGE,"E2.bottom")])]});var subQ12=makeQuery(id+"F1.opExtrude","SWEPT_FACE",FACE,{"disambiguationData":[OSD([sQuery(id+"F0.wireOp",EDGE,"E0.bottom")])]});var subQ14=makeQuery(id+"F1.opExtrude","SWEPT_FACE",FACE,{"disambiguationData":[OSD([sQuery(id+"F0.wireOp",EDGE,"E0.right")])]});var subQ19=makeQuery(id+"F5.boolean.opBoolean","MERGE",FACE,{"derivedFrom":[subQ5,subQ7]});Q0=makeQuery(id+"F39.boolean.opBoolean","MERGE",FACE,{"derivedFrom":[makeQuery(id+"F7.boolean.opBoolean","SPLIT",FACE,{"disambiguationData":[TD([subQ6])],"derivedFrom":subQ19}),makeQuery(id+"F22.boolean.opBoolean","SPLIT",FACE,{"disambiguationData":[TD([subQ2])],"derivedFrom":makeQuery(id+"F20.boolean.opBoolean","MERGE",FACE,{"derivedFrom":[makeQuery(id+"F7.boolean.opBoolean","SPLIT",FACE,{"disambiguationData":[TD([subQ14])],"derivedFrom":subQ19}),makeQuery(id+"F16.boolean.opBoolean","SPLIT",FACE,{"disambiguationData":[TD([subQ12])],"derivedFrom":makeQuery(id+"F7.boolean.opBoolean","SPLIT",FACE,{"disambiguationData":[TD([subQ12])],"derivedFrom":subQ19})}),makeQuery(id+"F20.opExtrude","SWEPT_FACE",FACE,{"disambiguationData":[OSD([sQuery(id+"F19.wireOp",EDGE,"E24.top")])]})]})}),makeQuery(id+"F39.opExtrude","SWEPT_FACE",FACE,{"disambiguationData":[OSD([sQuery(id+"F38.wireOp",EDGE,"E60.bottom")])]})]});}
            var sketch = newSketch(context, id + "F45", { "sketchPlane" : qUnion([Q0])});
            skLineSegment(sketch, "E63.bottom", {"start": v(127.32, 185.5) * mm, "end": v(124.32, 185.5) * mm});
            skLineSegment(sketch, "E63.top", {"start": v(127.32, -188.5) * mm, "end": v(124.32, -188.5) * mm});
            skLineSegment(sketch, "E63.left", {"start": v(127.32, 185.5) * mm, "end": v(127.32, -188.5) * mm});
            skLineSegment(sketch, "E63.right", {"start": v(124.32, 185.5) * mm, "end": v(124.32, -188.5) * mm});
            skSolve(sketch);
        }
        {
            var Q0;
            Q0 = qSketchRegion(id + "F45", true);
            extrude(context, id + "F46", {"entities" : qUnion([Q0]), "depth" : 300 * mm});
        }
        {
            var Q0;
            {var subQ4=makeQuery(id+"F12.opExtrude","SWEPT_FACE",FACE,{"disambiguationData":[OSD([sQuery(id+"F11.wireOp",EDGE,"E10.right")])]});Q0=makeQuery(id+"F32.boolean.opBoolean","MERGE",FACE,{"derivedFrom":[makeQuery(id+"F16.boolean.opBoolean","SPLIT",FACE,{"disambiguationData":[TD([makeQuery(id+"F12.opExtrude","SWEPT_FACE",FACE,{"disambiguationData":[OSD([sQuery(id+"F11.wireOp",EDGE,"E10.bottom")])]})])],"derivedFrom":subQ4}),makeQuery(id+"F16.boolean.opBoolean","SPLIT",FACE,{"disambiguationData":[TD([makeQuery(id+"F12.opExtrude","SWEPT_FACE",FACE,{"disambiguationData":[OSD([sQuery(id+"F11.wireOp",EDGE,"E10.top")])]})])],"derivedFrom":subQ4}),makeQuery(id+"F32.opExtrude","SWEPT_FACE",FACE,{"disambiguationData":[OSD([sQuery(id+"F31.wireOp",EDGE,"E47.right")])]})]});}
            var sketch = newSketch(context, id + "F47", { "sketchPlane" : qUnion([Q0])});
            skLineSegment(sketch, "E64.bottom", {"start": v(-136, 287.5) * mm, "end": v(-161, 287.5) * mm});
            skLineSegment(sketch, "E64.top", {"start": v(-136, 272.5) * mm, "end": v(-161, 272.5) * mm});
            skLineSegment(sketch, "E64.left", {"start": v(-136, 287.5) * mm, "end": v(-136, 272.5) * mm});
            skLineSegment(sketch, "E64.right", {"start": v(-161, 287.5) * mm, "end": v(-161, 272.5) * mm});
            skPoint(sketch, "E64.middle", {"position": v(-148.5, 280) * mm});
            skSolve(sketch);
        }
        {
            var Q0;
            Q0 = qSketchRegion(id + "F47", true);
            extrude(context, id + "F48", {"entities" : qUnion([Q0]), "operationType" : NewBodyOperationType.REMOVE, "oppositeDirection" : true, "depth" : 25 * mm});
        }
        {
            var Q0;
            Q0=makeQuery(id+"F48.boolean.opBoolean","COPY",EDGE,{"derivedFrom":makeQuery(id+"F48.opExtrude","SWEPT_EDGE",EDGE,{"disambiguationData":[OSD([sQuery(id+"F47.wireOp",EDGE,"E64.top"),sQuery(id+"F47.wireOp",EDGE,"E64.right")])]})});
            var Q1;
            Q1=makeQuery(id+"F48.boolean.opBoolean","COPY",EDGE,{"derivedFrom":makeQuery(id+"F48.opExtrude","SWEPT_EDGE",EDGE,{"disambiguationData":[OSD([sQuery(id+"F47.wireOp",EDGE,"E64.bottom"),sQuery(id+"F47.wireOp",EDGE,"E64.right")])]})});
            var Q2;
            Q2=makeQuery(id+"F48.boolean.opBoolean","COPY",EDGE,{"derivedFrom":makeQuery(id+"F48.opExtrude","SWEPT_EDGE",EDGE,{"disambiguationData":[OSD([sQuery(id+"F47.wireOp",EDGE,"E64.bottom"),sQuery(id+"F47.wireOp",EDGE,"E64.left")])]})});
            var Q3;
            Q3=makeQuery(id+"F48.boolean.opBoolean","COPY",EDGE,{"derivedFrom":makeQuery(id+"F48.opExtrude","SWEPT_EDGE",EDGE,{"disambiguationData":[OSD([sQuery(id+"F47.wireOp",EDGE,"E64.top"),sQuery(id+"F47.wireOp",EDGE,"E64.left")])]})});
            fillet(context, id + "F49", {"entities" : qUnion([Q0, Q1, Q2, Q3]), "radius" : 5 * mm, "tangentPropagation" : true, "allowEdgeOverflow" : false});
        }
        {
            var Q0;
            Q0=makeQuery(id+"F44.opExtrude","SWEPT_BODY",BODY,{"disambiguationData":[OSD([sQuery(id+"F43.wireOp",EDGE,"E62.bottom"),sQuery(id+"F43.wireOp",EDGE,"E62.top"),sQuery(id+"F43.wireOp",EDGE,"E62.left"),sQuery(id+"F43.wireOp",EDGE,"E62.right")])]});
            var Q1;
            Q1=makeQuery(id+"F46.opExtrude","SWEPT_BODY",BODY,{"disambiguationData":[OSD([sQuery(id+"F45.wireOp",EDGE,"E63.bottom"),sQuery(id+"F45.wireOp",EDGE,"E63.top"),sQuery(id+"F45.wireOp",EDGE,"E63.left"),sQuery(id+"F45.wireOp",EDGE,"E63.right")])]});
            deleteBodies(context, id + "F50", {"entities" : qUnion([Q0, Q1])});
        }
        {
            var Q0;
            Q0=makeQuery(id+"F12.opExtrude","SWEPT_FACE",FACE,{"disambiguationData":[OSD([sQuery(id+"F11.wireOp",EDGE,"E10.left")])]});
            var sketch = newSketch(context, id + "F51", { "sketchPlane" : qUnion([Q0])});
            skLineSegment(sketch, "E65.bottom", {"start": v(-75.5, 40.06) * mm, "end": v(-45.5, 40.06) * mm});
            skLineSegment(sketch, "E65.top", {"start": v(-75.5, 25.06) * mm, "end": v(-45.5, 25.06) * mm});
            skLineSegment(sketch, "E65.left", {"start": v(-75.5, 40.06) * mm, "end": v(-75.5, 25.06) * mm});
            skLineSegment(sketch, "E65.right", {"start": v(-45.5, 40.06) * mm, "end": v(-45.5, 25.06) * mm});
            skPoint(sketch, "E65.middle", {"position": v(-60.5, 32.56) * mm});
            skLineSegment(sketch, "E66", {"start": v(-75.5, 25.06) * mm, "end": v(-185.5, 25.06) * mm});
            skLineSegment(sketch, "E67", {"start": v(-45.5, 40.06) * mm, "end": v(-45.5, 240.06) * mm});
            skLineSegment(sketch, "E68.bottom", {"start": v(-45.5, 240.06) * mm, "end": v(-60.5, 240.06) * mm});
            skLineSegment(sketch, "E68.top", {"start": v(-45.5, 200.06) * mm, "end": v(-60.5, 200.06) * mm});
            skLineSegment(sketch, "E68.left", {"start": v(-45.5, 240.06) * mm, "end": v(-45.5, 200.06) * mm});
            skLineSegment(sketch, "E68.right", {"start": v(-60.5, 240.06) * mm, "end": v(-60.5, 200.06) * mm});
            skSolve(sketch);
        }
        {
            var Q0;
            Q0 = qSketchRegion(id + "F51", true);
            extrude(context, id + "F52", {"entities" : qUnion([Q0]), "operationType" : NewBodyOperationType.REMOVE, "oppositeDirection" : true, "depth" : 25 * mm});
        }
        {
            var Q0;
            Q0=makeQuery(id+"F52.boolean.opBoolean","COPY",EDGE,{"derivedFrom":makeQuery(id+"F52.opExtrude","SWEPT_EDGE",EDGE,{"disambiguationData":[OSD([sQuery(id+"F51.wireOp",EDGE,"E65.top"),sQuery(id+"F51.wireOp",EDGE,"E65.left")])]})});
            var Q1;
            Q1=makeQuery(id+"F52.boolean.opBoolean","COPY",EDGE,{"derivedFrom":makeQuery(id+"F52.opExtrude","SWEPT_EDGE",EDGE,{"disambiguationData":[OSD([sQuery(id+"F51.wireOp",EDGE,"E65.bottom"),sQuery(id+"F51.wireOp",EDGE,"E65.left")])]})});
            var Q2;
            Q2=makeQuery(id+"F52.boolean.opBoolean","COPY",EDGE,{"derivedFrom":makeQuery(id+"F52.opExtrude","SWEPT_EDGE",EDGE,{"disambiguationData":[OSD([sQuery(id+"F51.wireOp",EDGE,"E65.top"),sQuery(id+"F51.wireOp",EDGE,"E65.right")])]})});
            var Q3;
            Q3=makeQuery(id+"F52.boolean.opBoolean","COPY",EDGE,{"derivedFrom":makeQuery(id+"F52.opExtrude","SWEPT_EDGE",EDGE,{"disambiguationData":[OSD([sQuery(id+"F51.wireOp",EDGE,"E65.bottom"),sQuery(id+"F51.wireOp",EDGE,"E65.right")])]})});
            fillet(context, id + "F53", {"entities" : qUnion([Q0, Q1, Q2, Q3]), "radius" : 5 * mm, "tangentPropagation" : true, "allowEdgeOverflow" : false});
        }
        {
            var Q0;
            Q0=makeQuery(id+"F52.boolean.opBoolean","COPY",EDGE,{"derivedFrom":makeQuery(id+"F52.opExtrude","SWEPT_EDGE",EDGE,{"disambiguationData":[OSD([sQuery(id+"F51.wireOp",EDGE,"E68.top"),sQuery(id+"F51.wireOp",EDGE,"E68.right")])]})});
            var Q1;
            Q1=makeQuery(id+"F52.boolean.opBoolean","COPY",EDGE,{"derivedFrom":makeQuery(id+"F52.opExtrude","SWEPT_EDGE",EDGE,{"disambiguationData":[OSD([sQuery(id+"F51.wireOp",EDGE,"E68.top"),sQuery(id+"F51.wireOp",EDGE,"E68.left")])]})});
            var Q2;
            Q2=makeQuery(id+"F52.boolean.opBoolean","COPY",EDGE,{"derivedFrom":makeQuery(id+"F52.opExtrude","SWEPT_EDGE",EDGE,{"disambiguationData":[OSD([sQuery(id+"F51.wireOp",EDGE,"E68.bottom"),sQuery(id+"F51.wireOp",EDGE,"E68.left")])]})});
            var Q3;
            Q3=makeQuery(id+"F52.boolean.opBoolean","COPY",EDGE,{"derivedFrom":makeQuery(id+"F52.opExtrude","SWEPT_EDGE",EDGE,{"disambiguationData":[OSD([sQuery(id+"F51.wireOp",EDGE,"E68.bottom"),sQuery(id+"F51.wireOp",EDGE,"E68.right")])]})});
            fillet(context, id + "F54", {"entities" : qUnion([Q0, Q1, Q2, Q3]), "radius" : 5 * mm, "tangentPropagation" : true, "allowEdgeOverflow" : false});
        }
        {
            var Q0;
            Q0=makeQuery(id+"F1.opExtrude","SWEPT_FACE",FACE,{"disambiguationData":[OSD([sQuery(id+"F0.wireOp",EDGE,"E0.top")])]});
            var sketch = newSketch(context, id + "F55", { "sketchPlane" : qUnion([Q0])});
            skLineSegment(sketch, "E69.top", {"start": v(-130, 40) * mm, "end": v(-105, 40) * mm});
            skLineSegment(sketch, "E69.right", {"start": v(-105, 0) * mm, "end": v(-105, 40) * mm});
            skCircle(sketch, "E70", {"center": v(-105, 40) * mm, "radius": 4 * mm});
            skLineSegment(sketch, "E71.top", {"start": v(130, 40) * mm, "end": v(105, 40) * mm});
            skLineSegment(sketch, "E71.right", {"start": v(105, 0) * mm, "end": v(105, 40) * mm});
            skCircle(sketch, "E72", {"center": v(105, 40) * mm, "radius": 4 * mm});
            skLineSegment(sketch, "E73.top", {"start": v(130, 280) * mm, "end": v(105, 280) * mm});
            skLineSegment(sketch, "E73.right", {"start": v(105, 320) * mm, "end": v(105, 280) * mm});
            skCircle(sketch, "E74", {"center": v(105, 280) * mm, "radius": 4 * mm});
            skLineSegment(sketch, "E75.top", {"start": v(-130, 280) * mm, "end": v(-105, 280) * mm});
            skLineSegment(sketch, "E75.right", {"start": v(-105, 320) * mm, "end": v(-105, 280) * mm});
            skCircle(sketch, "E76", {"center": v(-105, 280) * mm, "radius": 4.5 * mm});
            skSolve(sketch);
        }
        {
            var Q0;
            Q0 = qSketchRegion(id + "F55", true);
            extrude(context, id + "F56", {"entities" : qUnion([Q0]), "operationType" : NewBodyOperationType.REMOVE, "oppositeDirection" : true, "depth" : 25 * mm});
        }
    });
